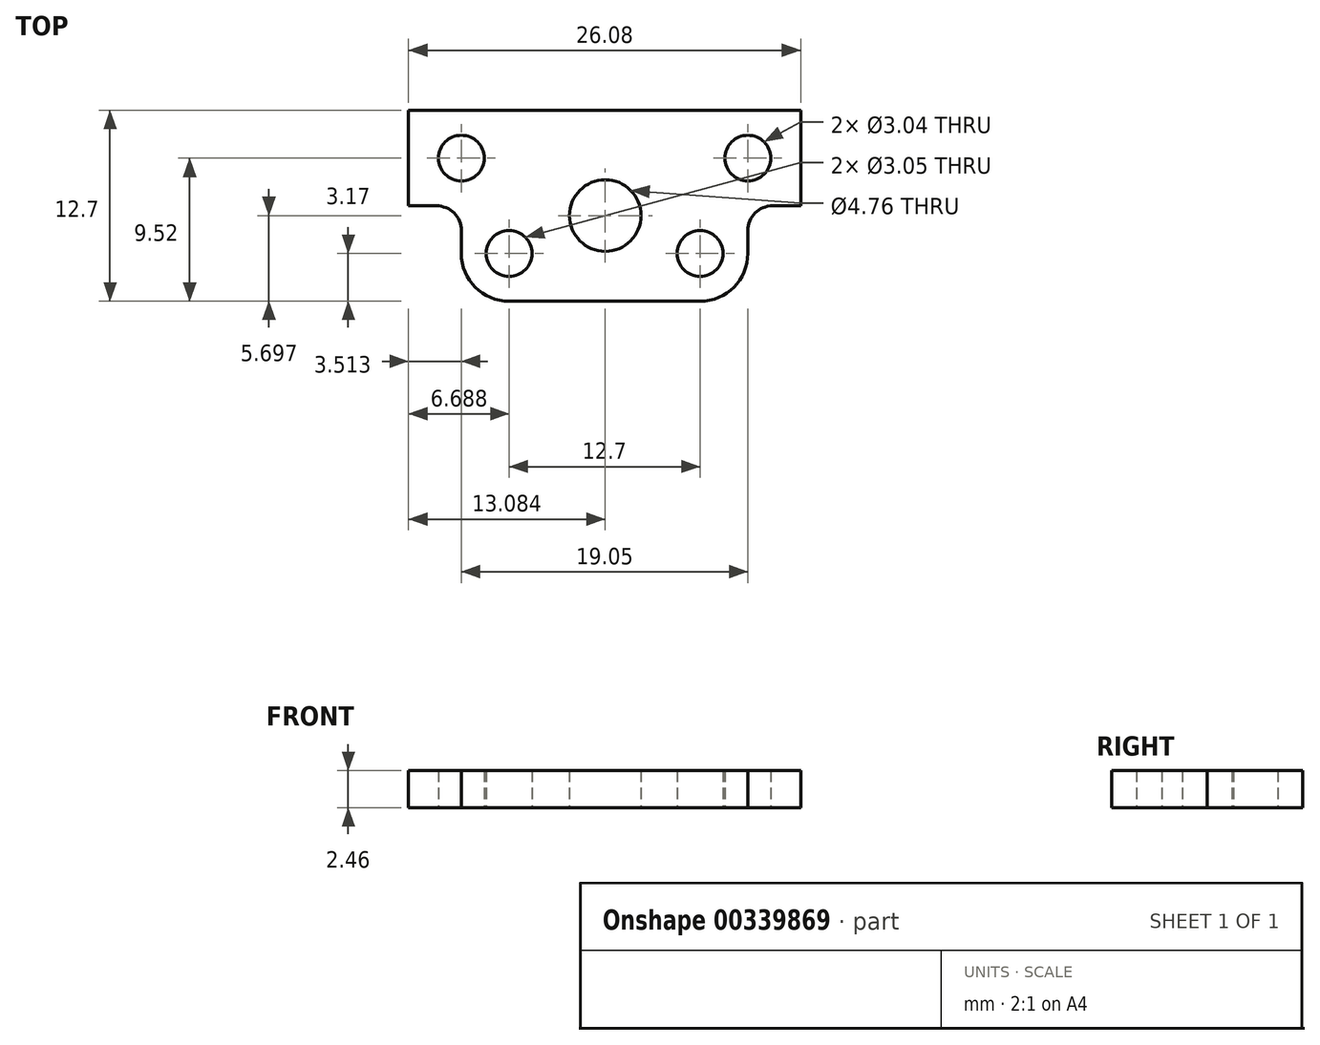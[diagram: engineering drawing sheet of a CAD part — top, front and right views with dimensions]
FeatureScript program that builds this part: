
annotation { "Feature Type Name" : "Feature", "Feature Type Description" : "" }
export const myFeature = defineFeature(function(context is Context, id is Id, definition is map)
    precondition{}
    {
        {
            var Q0;
            Q0=qCreatedBy(makeId("Top.planeOp"),FACE);
            var sketch = newSketch(context, id + "F0", { "sketchPlane" : qUnion([Q0])});
            skLineSegment(sketch, "E0.top", {"start": v(-18.33, 11.15) * mm, "end": v(-17.43, 11.15) * mm});
            skLineSegment(sketch, "E0.left", {"start": v(-21.5, 15.84) * mm, "end": v(-21.5, 14.32) * mm});
            skPoint(sketch, "E1", {"position": v(-5.63, 11.15) * mm});
            skPoint(sketch, "E2", {"position": v(-18.33, 11.15) * mm});
            skCircle(sketch, "E3", {"center": v(-18.33, 14.32) * mm, "radius": 1.52 * mm});
            skCircle(sketch, "E4", {"center": v(-5.63, 14.32) * mm, "radius": 1.52 * mm});
            skPoint(sketch, "E5.visualSharp", {"position": v(-21.5, 11.15) * mm});
            skArc(sketch, "E5.filletArc", {"start": v(-21.5, 14.32) * mm, "mid": v(-20.58, 12.07) * mm, "end": v(-18.33, 11.15) * mm});
            skPoint(sketch, "E6.visualSharp", {"position": v(-2.46, 11.15) * mm});
            skArc(sketch, "E6.filletArc", {"start": v(-5.63, 11.15) * mm, "mid": v(-3.39, 12.07) * mm, "end": v(-2.46, 14.32) * mm});
            skPoint(sketch, "E7.visualSharp", {"position": v(-2.46, 23.85) * mm});
            skPoint(sketch, "E8.visualSharp", {"position": v(-21.5, 23.85) * mm});
            skLineSegment(sketch, "E9", {"start": v(-23.16, 17.5) * mm, "end": v(-23.37, 17.5) * mm});
            skLineSegment(sketch, "E10", {"start": v(-25.02, 19.15) * mm, "end": v(-25.02, 22.2) * mm});
            skLineSegment(sketch, "E11", {"start": v(-23.37, 23.85) * mm, "end": v(-18.7, 23.85) * mm});
            skCircle(sketch, "E12", {"center": v(-21.5, 20.67) * mm, "radius": 1.52 * mm});
            skPoint(sketch, "E13.visualSharp", {"position": v(-21.5, 17.5) * mm});
            skArc(sketch, "E13.filletArc", {"start": v(-21.5, 15.84) * mm, "mid": v(-22, 17.01) * mm, "end": v(-23.16, 17.5) * mm});
            skPoint(sketch, "E14.visualSharp", {"position": v(-25.02, 17.5) * mm});
            skPoint(sketch, "E15.visualSharp", {"position": v(-25.02, 23.85) * mm});
            skLineSegment(sketch, "E16.MirrorCS", {"start": v(-0.6, 23.85) * mm, "end": v(-2.46, 23.85) * mm});
            skLineSegment(sketch, "E17.MirrorCS", {"start": v(1.06, 19.15) * mm, "end": v(1.06, 22.2) * mm});
            skCircle(sketch, "E18.MirrorC", {"center": v(-2.46, 20.67) * mm, "radius": 1.52 * mm});
            skArc(sketch, "E19.MirrorCS", {"start": v(-2.46, 15.84) * mm, "mid": v(-1.97, 17.01) * mm, "end": v(-0.8, 17.5) * mm});
            skLineSegment(sketch, "E20.trimOffspring", {"start": v(-2.46, 15.84) * mm, "end": v(-2.46, 14.32) * mm});
            skPoint(sketch, "E21.orphan", {"position": v(-11.98, 23.85) * mm});
            skCircle(sketch, "E22", {"center": v(-11.94, 16.85) * mm, "radius": 2.38 * mm});
            skLineSegment(sketch, "E23", {"start": v(-4.92, 23.85) * mm, "end": v(-2.46, 23.85) * mm});
            skLineSegment(sketch, "E24", {"start": v(-0.6, 17.5) * mm, "end": v(-0.8, 17.5) * mm});
            skPoint(sketch, "E25.end.orphan", {"position": v(-18.33, 20.86) * mm});
            skPoint(sketch, "E25.start.orphan", {"position": v(-18.33, 23.85) * mm});
            skPoint(sketch, "E26.end.orphan", {"position": v(-5.63, 23.85) * mm});
            skPoint(sketch, "E26.start.orphan", {"position": v(-5.63, 20.86) * mm});
            skLineSegment(sketch, "E27.trimOffspring", {"start": v(-6.54, 11.15) * mm, "end": v(-5.63, 11.15) * mm});
            skPoint(sketch, "E28.orphan", {"position": v(-11.98, 11.15) * mm});
            skPoint(sketch, "E29.visualSharp", {"position": v(-7.23, 11.15) * mm});
            skPoint(sketch, "E30.visualSharp", {"position": v(-16.73, 11.15) * mm});
            skPoint(sketch, "E31.start.orphan", {"position": v(-11.98, 20.86) * mm});
            skLineSegment(sketch, "E32", {"start": v(-18.7, 23.85) * mm, "end": v(-4.92, 23.85) * mm});
            skLineSegment(sketch, "E33", {"start": v(-23.37, 23.85) * mm, "end": v(-25.02, 23.85) * mm});
            skLineSegment(sketch, "E34", {"start": v(-25.02, 22.2) * mm, "end": v(-25.02, 23.85) * mm});
            skLineSegment(sketch, "E35", {"start": v(-17.43, 11.15) * mm, "end": v(-6.54, 11.15) * mm});
            skLineSegment(sketch, "E36", {"start": v(-0.6, 23.85) * mm, "end": v(1.06, 23.85) * mm});
            skLineSegment(sketch, "E37", {"start": v(1.06, 23.85) * mm, "end": v(1.06, 22.2) * mm});
            skLineSegment(sketch, "E38", {"start": v(1.06, 19.15) * mm, "end": v(1.06, 17.5) * mm});
            skLineSegment(sketch, "E39", {"start": v(1.06, 17.5) * mm, "end": v(-0.6, 17.5) * mm});
            skLineSegment(sketch, "E40", {"start": v(-23.16, 17.5) * mm, "end": v(-25.02, 17.5) * mm});
            skLineSegment(sketch, "E41", {"start": v(-25.02, 19.15) * mm, "end": v(-25.02, 17.5) * mm});
            skSolve(sketch);
        }
        {
            var Q0;
            Q0=makeQuery(id+"F0.imprint","IMPRINT",FACE,{"disambiguationData":[TD([[makeQuery(id+"F0.imprint","IMPRINT",EDGE,{"derivedFrom":sQuery(id+"F0.wireOp",EDGE,"E0.top")}),1.0]])]});
            extrude(context, id + "F1", {"entities" : qUnion([Q0]), "depth" : 2.46 * mm});
        }
    });
